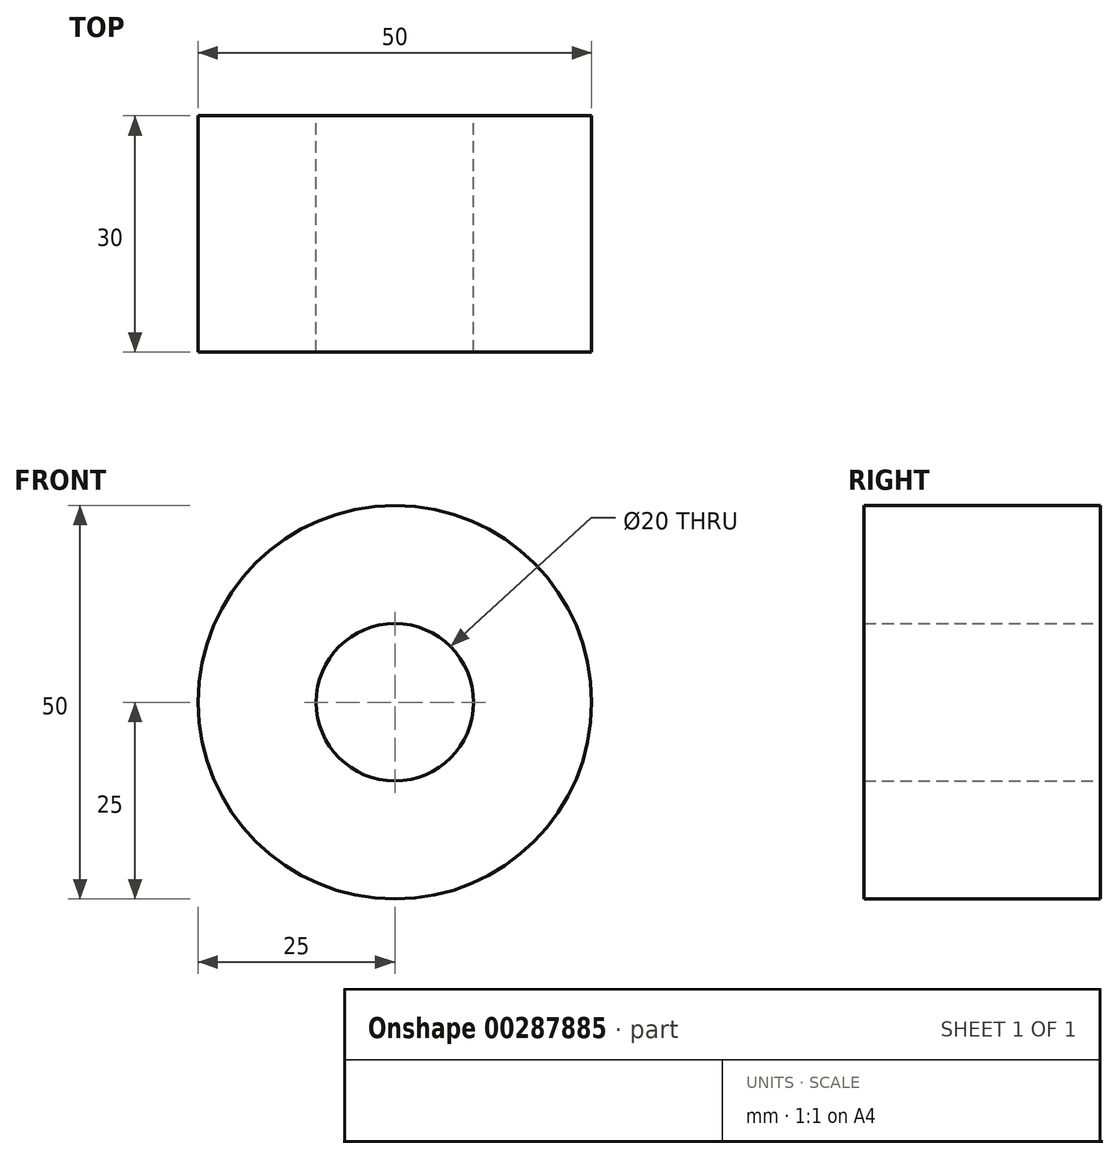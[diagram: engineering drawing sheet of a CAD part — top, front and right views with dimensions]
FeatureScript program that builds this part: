
annotation { "Feature Type Name" : "Feature", "Feature Type Description" : "" }
export const myFeature = defineFeature(function(context is Context, id is Id, definition is map)
    precondition{}
    {
        {
            var Q0;
            Q0=qCreatedBy(makeId("Front.planeOp"),FACE);
            var sketch = newSketch(context, id + "F0", { "sketchPlane" : qUnion([Q0])});
            skCircle(sketch, "E0", {"center": v(0, 0) * mm, "radius": 10 * mm});
            skCircle(sketch, "E1", {"center": v(0, 0) * mm, "radius": 25 * mm});
            skSolve(sketch);
        }
        {
            var Q0;
            Q0 = qSketchRegion(id + "F0", true);
            extrude(context, id + "F1", {"entities" : qUnion([Q0]), "depth" : 30 * mm});
        }
    });
